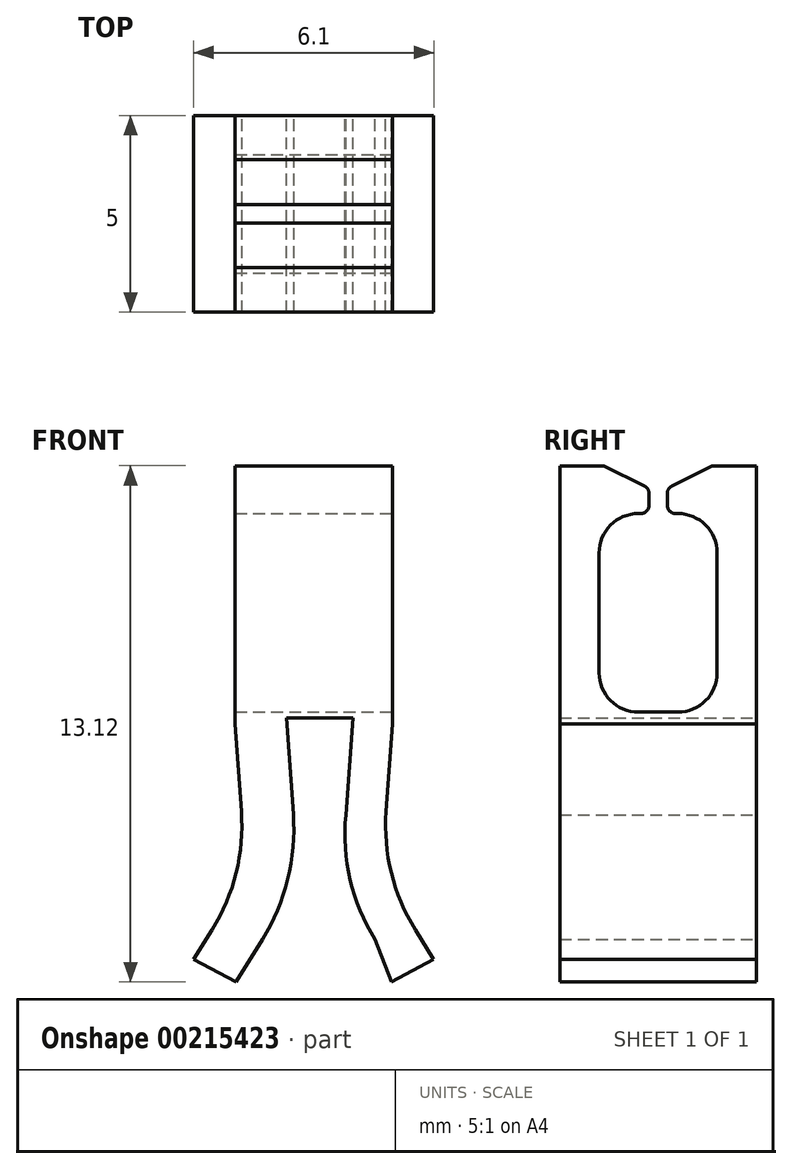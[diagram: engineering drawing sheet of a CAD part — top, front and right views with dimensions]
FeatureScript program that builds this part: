
annotation { "Feature Type Name" : "Feature", "Feature Type Description" : "" }
export const myFeature = defineFeature(function(context is Context, id is Id, definition is map)
    precondition{}
    {
        {
            var Q0;
            Q0=qCreatedBy(makeId("Front.planeOp"),FACE);
            var sketch = newSketch(context, id + "F0", { "sketchPlane" : qUnion([Q0])});
            skLineSegment(sketch, "E0.bottom", {"start": v(-1, -5) * mm, "end": v(1, -5) * mm, "construction": true});
            skLineSegment(sketch, "E0.top", {"start": v(-1, 5) * mm, "end": v(1, 5) * mm, "construction": true});
            skLineSegment(sketch, "E0.left", {"start": v(-1, -5) * mm, "end": v(-1, 5) * mm, "construction": true});
            skLineSegment(sketch, "E0.right", {"start": v(1, -5) * mm, "end": v(1, 5) * mm, "construction": true});
            skPoint(sketch, "E0.middle", {"position": v(0, 0) * mm});
            skLineSegment(sketch, "E1", {"start": v(-2, 13.12) * mm, "end": v(0, 13.12) * mm});
            skLineSegment(sketch, "E2", {"start": v(0, 13.12) * mm, "end": v(0, 0) * mm});
            skLineSegment(sketch, "E3.0", {"start": v(-2, 6.56) * mm, "end": v(-2, 13.12) * mm});
            skLineSegment(sketch, "E3.1", {"start": v(-1.84, 4.34) * mm, "end": v(-2, 6.56) * mm});
            skLineSegment(sketch, "E3.2", {"start": v(-3.05, 0.58) * mm, "end": v(-2.58, 1.33) * mm});
            skLineSegment(sketch, "E4", {"start": v(-1.98, 0) * mm, "end": v(-3.05, 0.58) * mm});
            skLineSegment(sketch, "E5", {"start": v(-0.7, 6.72) * mm, "end": v(0, 6.72) * mm});
            skPoint(sketch, "E6.visualSharp", {"position": v(-0.7, 2.46) * mm});
            skPoint(sketch, "E7.visualSharp", {"position": v(-1.72, 2.71) * mm});
            skArc(sketch, "E7.filletArc", {"start": v(-2.58, 1.33) * mm, "mid": v(-1.97, 2.78) * mm, "end": v(-1.84, 4.34) * mm});
            skArc(sketch, "E8.MirrorCS", {"start": v(1.56, 1.08) * mm, "mid": v(0.92, 2.6) * mm, "end": v(0.82, 4.24) * mm});
            skLineSegment(sketch, "E9.MirrorCS", {"start": v(1.98, 0) * mm, "end": v(1.56, 1.08) * mm});
            skLineSegment(sketch, "E10.MirrorCS", {"start": v(1.98, 0) * mm, "end": v(3.05, 0.58) * mm});
            skLineSegment(sketch, "E11.MirrorCS", {"start": v(3.05, 0.58) * mm, "end": v(2.58, 1.33) * mm});
            skArc(sketch, "E12.MirrorCS", {"start": v(2.58, 1.33) * mm, "mid": v(1.97, 2.78) * mm, "end": v(1.84, 4.34) * mm});
            skLineSegment(sketch, "E13.MirrorCS", {"start": v(0.82, 4.24) * mm, "end": v(1, 6.72) * mm});
            skLineSegment(sketch, "E14.MirrorCS", {"start": v(1.84, 4.34) * mm, "end": v(2, 6.56) * mm});
            skLineSegment(sketch, "E15.MirrorCS", {"start": v(1, 6.72) * mm, "end": v(0, 6.72) * mm});
            skLineSegment(sketch, "E16.MirrorCS", {"start": v(2, 6.56) * mm, "end": v(2, 13.12) * mm});
            skLineSegment(sketch, "E17.MirrorCS", {"start": v(2, 13.12) * mm, "end": v(0, 13.12) * mm});
            skLineSegment(sketch, "E18.0", {"start": v(-0.52, 4.26) * mm, "end": v(-0.7, 6.72) * mm});
            skArc(sketch, "E18.1", {"start": v(-1.3, 1.08) * mm, "mid": v(-0.66, 2.6) * mm, "end": v(-0.52, 4.26) * mm});
            skLineSegment(sketch, "E18.2", {"start": v(-1.98, 0) * mm, "end": v(-1.3, 1.08) * mm});
            skPoint(sketch, "E19.orphan", {"position": v(-1.56, 1.08) * mm});
            skPoint(sketch, "E20.start.orphan", {"position": v(-0.82, 4.24) * mm});
            skPoint(sketch, "E21.orphan", {"position": v(-1, 6.72) * mm});
            skSolve(sketch);
        }
        {
            var Q0;
            Q0 = qSketchRegion(id + "F0", true);
            extrude(context, id + "F1", {"entities" : qUnion([Q0]), "depth" : 5 * mm});
        }
        {
            var Q0;
            Q0=makeQuery(id+"F1.opExtrude","SWEPT_FACE",FACE,{"disambiguationData":[OSD([sQuery(id+"F0.wireOp",EDGE,"E16.MirrorCS")])]});
            var sketch = newSketch(context, id + "F2", { "sketchPlane" : qUnion([Q0])});
            skLineSegment(sketch, "E22", {"start": v(-2.5, 6.56) * mm, "end": v(-2.5, 13.12) * mm, "construction": true});
            skLineSegment(sketch, "E23", {"start": v(-2.73, 12.42) * mm, "end": v(-2.73, 12.1) * mm});
            skLineSegment(sketch, "E24", {"start": v(-2.93, 11.9) * mm, "end": v(-3, 11.9) * mm});
            skLineSegment(sketch, "E25", {"start": v(-4, 10.9) * mm, "end": v(-4, 7.86) * mm});
            skLineSegment(sketch, "E26", {"start": v(-3, 6.86) * mm, "end": v(-2.5, 6.86) * mm});
            skLineSegment(sketch, "E27", {"start": v(-2.84, 12.6) * mm, "end": v(-3.87, 13.12) * mm});
            skPoint(sketch, "E28.visualSharp", {"position": v(-4, 11.9) * mm});
            skArc(sketch, "E28.filletArc", {"start": v(-3, 11.9) * mm, "mid": v(-3.7, 11.61) * mm, "end": v(-4, 10.9) * mm});
            skPoint(sketch, "E29.visualSharp", {"position": v(-4, 6.86) * mm});
            skArc(sketch, "E29.filletArc", {"start": v(-4, 7.86) * mm, "mid": v(-3.7, 7.15) * mm, "end": v(-3, 6.86) * mm});
            skPoint(sketch, "E30.visualSharp", {"position": v(-2.73, 12.55) * mm});
            skArc(sketch, "E30.filletArc", {"start": v(-2.73, 12.42) * mm, "mid": v(-2.76, 12.53) * mm, "end": v(-2.84, 12.6) * mm});
            skPoint(sketch, "E31.visualSharp", {"position": v(-2.73, 11.9) * mm});
            skArc(sketch, "E31.filletArc", {"start": v(-2.93, 11.9) * mm, "mid": v(-2.8, 11.96) * mm, "end": v(-2.73, 12.1) * mm});
            skLineSegment(sketch, "E32", {"start": v(-3.87, 13.12) * mm, "end": v(-2.5, 13.12) * mm});
            skLineSegment(sketch, "E33.MirrorCS", {"start": v(-1.13, 13.12) * mm, "end": v(-2.5, 13.12) * mm});
            skLineSegment(sketch, "E34.MirrorCS", {"start": v(-2.16, 12.6) * mm, "end": v(-1.13, 13.12) * mm});
            skArc(sketch, "E35.MirrorCS", {"start": v(-2.27, 12.42) * mm, "mid": v(-2.24, 12.53) * mm, "end": v(-2.16, 12.6) * mm});
            skLineSegment(sketch, "E36.MirrorCS", {"start": v(-2.27, 12.42) * mm, "end": v(-2.27, 12.1) * mm});
            skArc(sketch, "E37.MirrorCS", {"start": v(-2.07, 11.9) * mm, "mid": v(-2.2, 11.96) * mm, "end": v(-2.27, 12.1) * mm});
            skArc(sketch, "E38.MirrorCS", {"start": v(-2, 11.9) * mm, "mid": v(-1.3, 11.61) * mm, "end": v(-1, 10.9) * mm});
            skLineSegment(sketch, "E39.MirrorCS", {"start": v(-2.07, 11.9) * mm, "end": v(-2, 11.9) * mm});
            skLineSegment(sketch, "E40.MirrorCS", {"start": v(-1, 10.9) * mm, "end": v(-1, 7.86) * mm});
            skArc(sketch, "E41.MirrorCS", {"start": v(-1, 7.86) * mm, "mid": v(-1.3, 7.15) * mm, "end": v(-2, 6.86) * mm});
            skLineSegment(sketch, "E42.MirrorCS", {"start": v(-2, 6.86) * mm, "end": v(-2.5, 6.86) * mm});
            skSolve(sketch);
        }
        {
            var Q0;
            Q0 = qSketchRegion(id + "F2", true);
            extrude(context, id + "F3", {"entities" : qUnion([Q0]), "operationType" : NewBodyOperationType.REMOVE, "endBound" : BoundingType.THROUGH_ALL, "oppositeDirection" : true, "depth" : 25 * mm});
        }
    });
